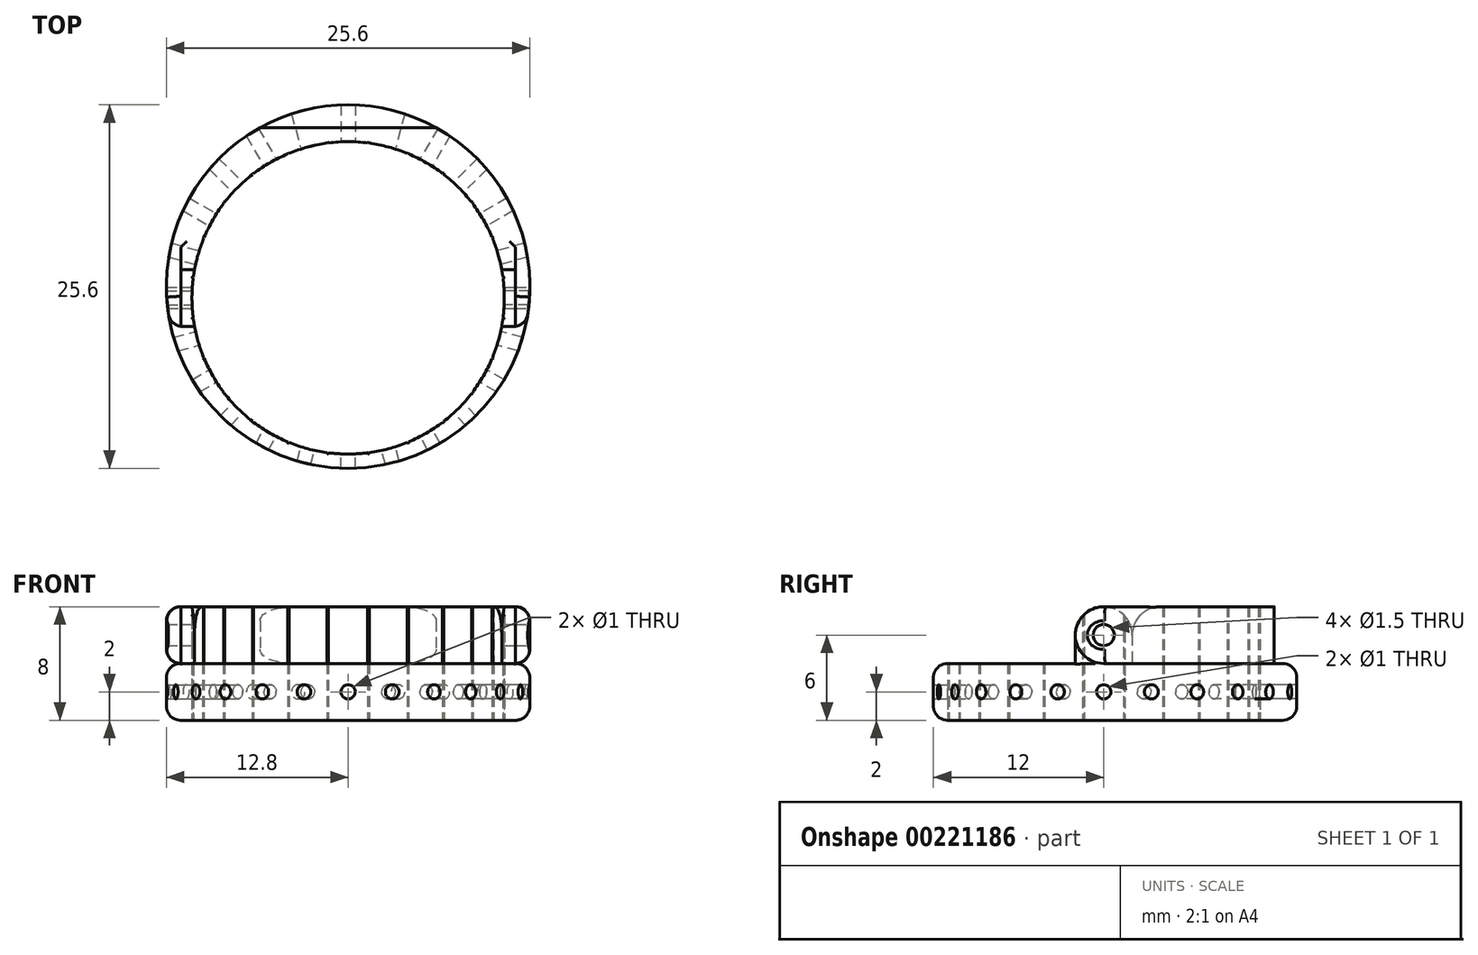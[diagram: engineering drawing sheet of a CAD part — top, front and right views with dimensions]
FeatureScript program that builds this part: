
annotation { "Feature Type Name" : "Feature", "Feature Type Description" : "" }
export const myFeature = defineFeature(function(context is Context, id is Id, definition is map)
    precondition{}
    {
        {
            var Q0;
            Q0=qCreatedBy(makeId("Top.planeOp"),FACE);
            var sketch = newSketch(context, id + "F0", { "sketchPlane" : qUnion([Q0])});
            skCircle(sketch, "E0", {"center": v(0, 0) * mm, "radius": 11 * mm});
            skCircle(sketch, "E1", {"center": v(0, 0) * mm, "radius": 12 * mm});
            skLineSegment(sketch, "E2", {"start": v(0, 0) * mm, "end": v(0, 0.8) * mm});
            skCircle(sketch, "E3", {"center": v(0, 0.8) * mm, "radius": 12.8 * mm});
            skLineSegment(sketch, "E4", {"start": v(0, 0) * mm, "end": v(-11, 0) * mm, "construction": true});
            skLineSegment(sketch, "E5", {"start": v(0, 0) * mm, "end": v(-10.9, 1.44) * mm, "construction": true});
            skLineSegment(sketch, "E6", {"start": v(-10.9, 1.44) * mm, "end": v(-11, 1.45) * mm, "construction": true});
            skLineSegment(sketch, "E7", {"start": v(-11, 1.45) * mm, "end": v(-10.9, 1.5) * mm});
            skLineSegment(sketch, "E8.MirrorCS", {"start": v(-11, 1.45) * mm, "end": v(-10.91, 1.38) * mm});
            skLineSegment(sketch, "E9.1.0", {"start": v(-11, -1.45) * mm, "end": v(-10.91, -1.38) * mm});
            skLineSegment(sketch, "E9.1.1", {"start": v(-11, -1.45) * mm, "end": v(-10.9, -1.5) * mm});
            skLineSegment(sketch, "E9.2.0", {"start": v(-10.26, -4.25) * mm, "end": v(-10.18, -4.16) * mm});
            skLineSegment(sketch, "E9.2.1", {"start": v(-10.26, -4.25) * mm, "end": v(-10.14, -4.26) * mm});
            skLineSegment(sketch, "E9.3.0", {"start": v(-8.8, -6.76) * mm, "end": v(-8.76, -6.65) * mm});
            skLineSegment(sketch, "E9.3.1", {"start": v(-8.8, -6.76) * mm, "end": v(-8.7, -6.74) * mm});
            skLineSegment(sketch, "E9.4.0", {"start": v(-6.76, -8.8) * mm, "end": v(-6.74, -8.7) * mm});
            skLineSegment(sketch, "E9.4.1", {"start": v(-6.76, -8.8) * mm, "end": v(-6.65, -8.76) * mm});
            skLineSegment(sketch, "E9.5.0", {"start": v(-4.25, -10.26) * mm, "end": v(-4.26, -10.14) * mm});
            skLineSegment(sketch, "E9.5.1", {"start": v(-4.25, -10.26) * mm, "end": v(-4.16, -10.18) * mm});
            skLineSegment(sketch, "E9.6.0", {"start": v(-1.45, -11) * mm, "end": v(-1.5, -10.9) * mm});
            skLineSegment(sketch, "E9.6.1", {"start": v(-1.45, -11) * mm, "end": v(-1.38, -10.91) * mm});
            skLineSegment(sketch, "E9.7.0", {"start": v(1.45, -11) * mm, "end": v(1.38, -10.91) * mm});
            skLineSegment(sketch, "E9.7.1", {"start": v(1.45, -11) * mm, "end": v(1.5, -10.9) * mm});
            skLineSegment(sketch, "E9.8.0", {"start": v(4.25, -10.26) * mm, "end": v(4.16, -10.18) * mm});
            skLineSegment(sketch, "E9.8.1", {"start": v(4.25, -10.26) * mm, "end": v(4.26, -10.14) * mm});
            skLineSegment(sketch, "E9.9.0", {"start": v(6.76, -8.8) * mm, "end": v(6.65, -8.76) * mm});
            skLineSegment(sketch, "E9.9.1", {"start": v(6.76, -8.8) * mm, "end": v(6.74, -8.7) * mm});
            skLineSegment(sketch, "E9.10.0", {"start": v(8.8, -6.76) * mm, "end": v(8.7, -6.74) * mm});
            skLineSegment(sketch, "E9.10.1", {"start": v(8.8, -6.76) * mm, "end": v(8.76, -6.65) * mm});
            skLineSegment(sketch, "E9.11.0", {"start": v(10.26, -4.25) * mm, "end": v(10.14, -4.26) * mm});
            skLineSegment(sketch, "E9.11.1", {"start": v(10.26, -4.25) * mm, "end": v(10.18, -4.16) * mm});
            skLineSegment(sketch, "E9.12.0", {"start": v(11, -1.45) * mm, "end": v(10.9, -1.5) * mm});
            skLineSegment(sketch, "E9.12.1", {"start": v(11, -1.45) * mm, "end": v(10.91, -1.38) * mm});
            skLineSegment(sketch, "E9.13.0", {"start": v(11, 1.45) * mm, "end": v(10.91, 1.38) * mm});
            skLineSegment(sketch, "E9.13.1", {"start": v(11, 1.45) * mm, "end": v(10.9, 1.5) * mm});
            skLineSegment(sketch, "E9.14.0", {"start": v(10.26, 4.25) * mm, "end": v(10.18, 4.16) * mm});
            skLineSegment(sketch, "E9.14.1", {"start": v(10.26, 4.25) * mm, "end": v(10.14, 4.26) * mm});
            skLineSegment(sketch, "E9.15.0", {"start": v(8.8, 6.76) * mm, "end": v(8.76, 6.65) * mm});
            skLineSegment(sketch, "E9.15.1", {"start": v(8.8, 6.76) * mm, "end": v(8.7, 6.74) * mm});
            skLineSegment(sketch, "E9.16.0", {"start": v(6.76, 8.8) * mm, "end": v(6.74, 8.7) * mm});
            skLineSegment(sketch, "E9.16.1", {"start": v(6.76, 8.8) * mm, "end": v(6.65, 8.76) * mm});
            skLineSegment(sketch, "E9.17.0", {"start": v(4.25, 10.26) * mm, "end": v(4.26, 10.14) * mm});
            skLineSegment(sketch, "E9.17.1", {"start": v(4.25, 10.26) * mm, "end": v(4.16, 10.18) * mm});
            skLineSegment(sketch, "E9.18.0", {"start": v(1.45, 11) * mm, "end": v(1.5, 10.9) * mm});
            skLineSegment(sketch, "E9.18.1", {"start": v(1.45, 11) * mm, "end": v(1.38, 10.91) * mm});
            skLineSegment(sketch, "E9.19.0", {"start": v(-1.45, 11) * mm, "end": v(-1.38, 10.91) * mm});
            skLineSegment(sketch, "E9.19.1", {"start": v(-1.45, 11) * mm, "end": v(-1.5, 10.9) * mm});
            skLineSegment(sketch, "E9.20.0", {"start": v(-4.25, 10.26) * mm, "end": v(-4.16, 10.18) * mm});
            skLineSegment(sketch, "E9.20.1", {"start": v(-4.25, 10.26) * mm, "end": v(-4.26, 10.14) * mm});
            skLineSegment(sketch, "E9.21.0", {"start": v(-6.76, 8.8) * mm, "end": v(-6.65, 8.76) * mm});
            skLineSegment(sketch, "E9.21.1", {"start": v(-6.76, 8.8) * mm, "end": v(-6.74, 8.7) * mm});
            skLineSegment(sketch, "E9.22.0", {"start": v(-8.8, 6.76) * mm, "end": v(-8.7, 6.74) * mm});
            skLineSegment(sketch, "E9.22.1", {"start": v(-8.8, 6.76) * mm, "end": v(-8.76, 6.65) * mm});
            skLineSegment(sketch, "E9.23.0", {"start": v(-10.26, 4.25) * mm, "end": v(-10.14, 4.26) * mm});
            skLineSegment(sketch, "E9.23.1", {"start": v(-10.26, 4.25) * mm, "end": v(-10.18, 4.16) * mm});
            skLineSegment(sketch, "E10.bottom", {"start": v(0, 10) * mm, "end": v(0.5, 10) * mm});
            skLineSegment(sketch, "E10.top", {"start": v(0, 14) * mm, "end": v(0.5, 14) * mm});
            skLineSegment(sketch, "E10.left", {"start": v(0, 10) * mm, "end": v(0, 14) * mm});
            skLineSegment(sketch, "E10.right", {"start": v(0.5, 10) * mm, "end": v(0.5, 14) * mm});
            skLineSegment(sketch, "E11", {"start": v(0, 0) * mm, "end": v(0, 2) * mm, "construction": true});
            skLineSegment(sketch, "E12", {"start": v(0, 2) * mm, "end": v(-10.82, 2) * mm, "construction": true});
            skLineSegment(sketch, "E13", {"start": v(-10.82, 2) * mm, "end": v(-12.74, 2) * mm});
            skLineSegment(sketch, "E14.MirrorCS", {"start": v(-10.82, -2) * mm, "end": v(-12.49, -2) * mm});
            skLineSegment(sketch, "E15.MirrorCS", {"start": v(10.82, -2) * mm, "end": v(12.49, -2) * mm});
            skLineSegment(sketch, "E16.MirrorCS", {"start": v(10.82, 2) * mm, "end": v(12.74, 2) * mm});
            skLineSegment(sketch, "E17", {"start": v(0, 12) * mm, "end": v(6.2, 12) * mm});
            skLineSegment(sketch, "E18.MirrorCS", {"start": v(0, 12) * mm, "end": v(-6.2, 12) * mm});
            skLineSegment(sketch, "E19", {"start": v(-11.78, 2) * mm, "end": v(-11.78, -2) * mm});
            skLineSegment(sketch, "E20.MirrorCS", {"start": v(11.78, 2) * mm, "end": v(11.78, -2) * mm});
            skLineSegment(sketch, "E21", {"start": v(0, 0) * mm, "end": v(0, -0.5) * mm, "construction": true});
            skLineSegment(sketch, "E22", {"start": v(0, -0.5) * mm, "end": v(-11.78, -0.5) * mm, "construction": true});
            skLineSegment(sketch, "E23", {"start": v(-11.78, -0.5) * mm, "end": v(-12.73, -0.5) * mm});
            skLineSegment(sketch, "E24", {"start": v(-11.78, 0) * mm, "end": v(-12.77, 0) * mm});
            skLineSegment(sketch, "E25.MirrorCS", {"start": v(11.78, 0) * mm, "end": v(12.77, 0) * mm});
            skLineSegment(sketch, "E26.MirrorCS", {"start": v(11.78, -0.5) * mm, "end": v(12.73, -0.5) * mm});
            skSolve(sketch);
        }
        {
            var Q0;
            {var subQ0=sQuery(id+"F0.wireOp",EDGE,"E17");var subQ1=sQuery(id+"F0.wireOp",EDGE,"E3");var subQ2=makeQuery(id+"F0.imprint","INTERSECT",VERTEX,{"derivedFrom":[subQ1,subQ0]});Q0=makeQuery(id+"F0.imprint","IMPRINT",FACE,{"disambiguationData":[TD([[makeQuery(id+"F0.imprint","IMPRINT",EDGE,{"disambiguationData":[TD([[subQ2,-1.0]])],"derivedFrom":subQ1}),1.0]])]});}
            var Q1;
            {var subQ0=sQuery(id+"F0.wireOp",EDGE,"E10.right");var subQ1=sQuery(id+"F0.wireOp",EDGE,"E3");var subQ2=makeQuery(id+"F0.imprint","INTERSECT",VERTEX,{"derivedFrom":[subQ1,subQ0]});Q1=makeQuery(id+"F0.imprint","IMPRINT",FACE,{"disambiguationData":[TD([[makeQuery(id+"F0.imprint","IMPRINT",EDGE,{"disambiguationData":[TD([[subQ2,-1.0]])],"derivedFrom":subQ1}),1.0]])]});}
            var Q2;
            {var subQ0=sQuery(id+"F0.wireOp",EDGE,"E18.MirrorCS");Q2=makeQuery(id+"F0.imprint","IMPRINT",FACE,{"disambiguationData":[TD([[makeQuery(id+"F0.imprint","IMPRINT",EDGE,{"derivedFrom":subQ0}),-1.0]])]});}
            var Q3;
            {var subQ0=sQuery(id+"F0.wireOp",EDGE,"E18.MirrorCS");Q3=makeQuery(id+"F0.imprint","IMPRINT",FACE,{"disambiguationData":[TD([[makeQuery(id+"F0.imprint","IMPRINT",EDGE,{"derivedFrom":subQ0}),1.0]])]});}
            var Q4;
            {var subQ12=sQuery(id+"F0.wireOp",EDGE,"E9.19.0");Q4=makeQuery(id+"F0.imprint","IMPRINT",FACE,{"disambiguationData":[TD([[makeQuery(id+"F0.imprint","IMPRINT",EDGE,{"derivedFrom":subQ12}),1.0]])]});}
            var Q5;
            {var subQ0=sQuery(id+"F0.wireOp",EDGE,"E16.MirrorCS");var subQ3=sQuery(id+"F0.wireOp",EDGE,"E1");var subQ4=makeQuery(id+"F0.imprint","INTERSECT",VERTEX,{"derivedFrom":[subQ3,subQ0]});Q5=makeQuery(id+"F0.imprint","IMPRINT",FACE,{"disambiguationData":[TD([[makeQuery(id+"F0.imprint","IMPRINT",EDGE,{"disambiguationData":[TD([[subQ4,-1.0]])],"derivedFrom":subQ3}),-1.0]])]});}
            var Q6;
            {var subQ1=sQuery(id+"F0.wireOp",EDGE,"E9.14.0");Q6=makeQuery(id+"F0.imprint","IMPRINT",FACE,{"disambiguationData":[TD([[makeQuery(id+"F0.imprint","IMPRINT",EDGE,{"derivedFrom":subQ1}),1.0]])]});}
            var Q7;
            {var subQ12=sQuery(id+"F0.wireOp",EDGE,"E9.12.0");Q7=makeQuery(id+"F0.imprint","IMPRINT",FACE,{"disambiguationData":[TD([[makeQuery(id+"F0.imprint","IMPRINT",EDGE,{"derivedFrom":subQ12}),1.0]])]});}
            var Q8;
            {var subQ0=sQuery(id+"F0.wireOp",EDGE,"E16.MirrorCS");var subQ1=sQuery(id+"F0.wireOp",EDGE,"E1");var subQ2=makeQuery(id+"F0.imprint","INTERSECT",VERTEX,{"derivedFrom":[subQ1,subQ0]});Q8=makeQuery(id+"F0.imprint","IMPRINT",FACE,{"disambiguationData":[TD([[makeQuery(id+"F0.imprint","IMPRINT",EDGE,{"disambiguationData":[TD([[subQ2,1.0]])],"derivedFrom":subQ1}),1.0]])]});}
            var Q9;
            {var subQ0=sQuery(id+"F0.wireOp",EDGE,"E16.MirrorCS");var subQ1=sQuery(id+"F0.wireOp",EDGE,"E1");var subQ2=makeQuery(id+"F0.imprint","INTERSECT",VERTEX,{"derivedFrom":[subQ1,subQ0]});Q9=makeQuery(id+"F0.imprint","IMPRINT",FACE,{"disambiguationData":[TD([[makeQuery(id+"F0.imprint","IMPRINT",EDGE,{"disambiguationData":[TD([[subQ2,1.0]])],"derivedFrom":subQ1}),-1.0]])]});}
            var Q10;
            {var subQ0=sQuery(id+"F0.wireOp",EDGE,"E25.MirrorCS");var subQ1=sQuery(id+"F0.wireOp",EDGE,"E1");var subQ2=makeQuery(id+"F0.imprint","INTERSECT",VERTEX,{"derivedFrom":[subQ1,subQ0]});Q10=makeQuery(id+"F0.imprint","IMPRINT",FACE,{"disambiguationData":[TD([[makeQuery(id+"F0.imprint","IMPRINT",EDGE,{"disambiguationData":[TD([[subQ2,1.0]])],"derivedFrom":subQ1}),-1.0]])]});}
            var Q11;
            {var subQ0=sQuery(id+"F0.wireOp",EDGE,"E15.MirrorCS");var subQ1=sQuery(id+"F0.wireOp",EDGE,"E1");var subQ2=makeQuery(id+"F0.imprint","INTERSECT",VERTEX,{"derivedFrom":[subQ1,subQ0]});Q11=makeQuery(id+"F0.imprint","IMPRINT",FACE,{"disambiguationData":[TD([[makeQuery(id+"F0.imprint","IMPRINT",EDGE,{"disambiguationData":[TD([[subQ2,-1.0]])],"derivedFrom":subQ1}),-1.0]])]});}
            var Q12;
            {var subQ0=sQuery(id+"F0.wireOp",EDGE,"E15.MirrorCS");var subQ1=sQuery(id+"F0.wireOp",EDGE,"E1");var subQ2=makeQuery(id+"F0.imprint","INTERSECT",VERTEX,{"derivedFrom":[subQ1,subQ0]});Q12=makeQuery(id+"F0.imprint","IMPRINT",FACE,{"disambiguationData":[TD([[makeQuery(id+"F0.imprint","IMPRINT",EDGE,{"disambiguationData":[TD([[subQ2,-1.0]])],"derivedFrom":subQ1}),1.0]])]});}
            var Q13;
            {var subQ0=sQuery(id+"F0.wireOp",EDGE,"E25.MirrorCS");var subQ1=sQuery(id+"F0.wireOp",EDGE,"E1");var subQ2=makeQuery(id+"F0.imprint","INTERSECT",VERTEX,{"derivedFrom":[subQ1,subQ0]});Q13=makeQuery(id+"F0.imprint","IMPRINT",FACE,{"disambiguationData":[TD([[makeQuery(id+"F0.imprint","IMPRINT",EDGE,{"disambiguationData":[TD([[subQ2,1.0]])],"derivedFrom":subQ1}),1.0]])]});}
            var Q14;
            {var subQ6=sQuery(id+"F0.wireOp",EDGE,"E9.2.0");Q14=makeQuery(id+"F0.imprint","IMPRINT",FACE,{"disambiguationData":[TD([[makeQuery(id+"F0.imprint","IMPRINT",EDGE,{"derivedFrom":subQ6}),1.0]])]});}
            var Q15;
            {var subQ0=sQuery(id+"F0.wireOp",EDGE,"E3");var subQ1=sQuery(id+"F0.wireOp",EDGE,"E1");var subQ2=makeQuery(id+"F0.imprint","INTERSECT",VERTEX,{"derivedFrom":[subQ1,subQ0]});Q15=makeQuery(id+"F0.imprint","IMPRINT",FACE,{"disambiguationData":[TD([[makeQuery(id+"F0.imprint","IMPRINT",EDGE,{"disambiguationData":[TD([[subQ2,-1.0]])],"derivedFrom":subQ1}),-1.0]])]});}
            var Q16;
            {var subQ0=sQuery(id+"F0.wireOp",EDGE,"E3");var subQ1=sQuery(id+"F0.wireOp",EDGE,"E1");var subQ2=makeQuery(id+"F0.imprint","INTERSECT",VERTEX,{"derivedFrom":[subQ1,subQ0]});Q16=makeQuery(id+"F0.imprint","IMPRINT",FACE,{"disambiguationData":[TD([[makeQuery(id+"F0.imprint","IMPRINT",EDGE,{"disambiguationData":[TD([[subQ2,1.0]])],"derivedFrom":subQ1}),-1.0]])]});}
            var Q17;
            {var subQ0=sQuery(id+"F0.wireOp",EDGE,"E23");var subQ1=sQuery(id+"F0.wireOp",EDGE,"E1");var subQ2=makeQuery(id+"F0.imprint","INTERSECT",VERTEX,{"derivedFrom":[subQ1,subQ0]});Q17=makeQuery(id+"F0.imprint","IMPRINT",FACE,{"disambiguationData":[TD([[makeQuery(id+"F0.imprint","IMPRINT",EDGE,{"disambiguationData":[TD([[subQ2,-1.0]])],"derivedFrom":subQ1}),-1.0]])]});}
            var Q18;
            {var subQ6=sQuery(id+"F0.wireOp",EDGE,"E7");Q18=makeQuery(id+"F0.imprint","IMPRINT",FACE,{"disambiguationData":[TD([[makeQuery(id+"F0.imprint","IMPRINT",EDGE,{"derivedFrom":subQ6}),1.0]])]});}
            var Q19;
            {var subQ0=sQuery(id+"F0.wireOp",EDGE,"E23");var subQ1=sQuery(id+"F0.wireOp",EDGE,"E1");var subQ2=makeQuery(id+"F0.imprint","INTERSECT",VERTEX,{"derivedFrom":[subQ1,subQ0]});Q19=makeQuery(id+"F0.imprint","IMPRINT",FACE,{"disambiguationData":[TD([[makeQuery(id+"F0.imprint","IMPRINT",EDGE,{"disambiguationData":[TD([[subQ2,-1.0]])],"derivedFrom":subQ1}),1.0]])]});}
            var Q20;
            {var subQ0=sQuery(id+"F0.wireOp",EDGE,"E24");var subQ1=sQuery(id+"F0.wireOp",EDGE,"E1");var subQ2=makeQuery(id+"F0.imprint","INTERSECT",VERTEX,{"derivedFrom":[subQ1,subQ0]});Q20=makeQuery(id+"F0.imprint","IMPRINT",FACE,{"disambiguationData":[TD([[makeQuery(id+"F0.imprint","IMPRINT",EDGE,{"disambiguationData":[TD([[subQ2,-1.0]])],"derivedFrom":subQ1}),1.0]])]});}
            var Q21;
            {var subQ0=sQuery(id+"F0.wireOp",EDGE,"E13");var subQ1=sQuery(id+"F0.wireOp",EDGE,"E1");var subQ2=makeQuery(id+"F0.imprint","INTERSECT",VERTEX,{"derivedFrom":[subQ1,subQ0]});Q21=makeQuery(id+"F0.imprint","IMPRINT",FACE,{"disambiguationData":[TD([[makeQuery(id+"F0.imprint","IMPRINT",EDGE,{"disambiguationData":[TD([[subQ2,-1.0]])],"derivedFrom":subQ1}),1.0]])]});}
            var Q22;
            {var subQ0=sQuery(id+"F0.wireOp",EDGE,"E13");var subQ1=sQuery(id+"F0.wireOp",EDGE,"E1");var subQ2=makeQuery(id+"F0.imprint","INTERSECT",VERTEX,{"derivedFrom":[subQ1,subQ0]});Q22=makeQuery(id+"F0.imprint","IMPRINT",FACE,{"disambiguationData":[TD([[makeQuery(id+"F0.imprint","IMPRINT",EDGE,{"disambiguationData":[TD([[subQ2,-1.0]])],"derivedFrom":subQ1}),-1.0]])]});}
            var Q23;
            {var subQ0=sQuery(id+"F0.wireOp",EDGE,"E24");var subQ1=sQuery(id+"F0.wireOp",EDGE,"E1");var subQ2=makeQuery(id+"F0.imprint","INTERSECT",VERTEX,{"derivedFrom":[subQ1,subQ0]});Q23=makeQuery(id+"F0.imprint","IMPRINT",FACE,{"disambiguationData":[TD([[makeQuery(id+"F0.imprint","IMPRINT",EDGE,{"disambiguationData":[TD([[subQ2,-1.0]])],"derivedFrom":subQ1}),-1.0]])]});}
            var Q24;
            {var subQ0=sQuery(id+"F0.wireOp",EDGE,"E10.right");var subQ1=sQuery(id+"F0.wireOp",EDGE,"E0");var subQ2=makeQuery(id+"F0.imprint","INTERSECT",VERTEX,{"derivedFrom":[subQ1,subQ0]});Q24=makeQuery(id+"F0.imprint","IMPRINT",FACE,{"disambiguationData":[TD([[makeQuery(id+"F0.imprint","IMPRINT",EDGE,{"disambiguationData":[TD([[subQ2,-1.0]])],"derivedFrom":subQ1}),-1.0]])]});}
            var Q25;
            {var subQ1=sQuery(id+"F0.wireOp",EDGE,"E1");var subQ3=sQuery(id+"F0.wireOp",EDGE,"E10.right");var subQ4=makeQuery(id+"F0.imprint","INTERSECT",VERTEX,{"derivedFrom":[subQ1,subQ3]});Q25=makeQuery(id+"F0.imprint","IMPRINT",FACE,{"disambiguationData":[TD([[makeQuery(id+"F0.imprint","IMPRINT",EDGE,{"disambiguationData":[TD([[subQ4,-1.0]])],"derivedFrom":subQ3}),1.0]])]});}
            extrude(context, id + "F1", {"entities" : qUnion([Q0, Q1, Q2, Q3, Q4, Q5, Q6, Q7, Q8, Q9, Q10, Q11, Q12, Q13, Q14, Q15, Q16, Q17, Q18, Q19, Q20, Q21, Q22, Q23, Q24, Q25]), "endBound" : BoundingType.SYMMETRIC, "depth" : 4 * mm});
        }
        {
            var Q0;
            {var subQ5=sQuery(id+"F0.wireOp",EDGE,"E10.top");Q0=makeQuery(id+"F0.imprint","IMPRINT",FACE,{"disambiguationData":[TD([[makeQuery(id+"F0.imprint","IMPRINT",EDGE,{"derivedFrom":subQ5}),-1.0]])]});}
            var Q1;
            {var subQ0=sQuery(id+"F0.wireOp",EDGE,"E10.right");var subQ1=sQuery(id+"F0.wireOp",EDGE,"E3");var subQ2=makeQuery(id+"F0.imprint","INTERSECT",VERTEX,{"derivedFrom":[subQ1,subQ0]});Q1=makeQuery(id+"F0.imprint","IMPRINT",FACE,{"disambiguationData":[TD([[makeQuery(id+"F0.imprint","IMPRINT",EDGE,{"disambiguationData":[TD([[subQ2,-1.0]])],"derivedFrom":subQ1}),1.0]])]});}
            var Q2;
            {var subQ0=sQuery(id+"F0.wireOp",EDGE,"E10.right");var subQ1=sQuery(id+"F0.wireOp",EDGE,"E0");var subQ2=makeQuery(id+"F0.imprint","INTERSECT",VERTEX,{"derivedFrom":[subQ1,subQ0]});Q2=makeQuery(id+"F0.imprint","IMPRINT",FACE,{"disambiguationData":[TD([[makeQuery(id+"F0.imprint","IMPRINT",EDGE,{"disambiguationData":[TD([[subQ2,-1.0]])],"derivedFrom":subQ1}),-1.0]])]});}
            var Q3;
            {var subQ5=sQuery(id+"F0.wireOp",EDGE,"E10.bottom");Q3=makeQuery(id+"F0.imprint","IMPRINT",FACE,{"disambiguationData":[TD([[makeQuery(id+"F0.imprint","IMPRINT",EDGE,{"derivedFrom":subQ5}),1.0]])]});}
            var Q4;
            {var subQ1=sQuery(id+"F0.wireOp",EDGE,"E1");var subQ3=sQuery(id+"F0.wireOp",EDGE,"E10.right");var subQ4=makeQuery(id+"F0.imprint","INTERSECT",VERTEX,{"derivedFrom":[subQ1,subQ3]});Q4=makeQuery(id+"F0.imprint","IMPRINT",FACE,{"disambiguationData":[TD([[makeQuery(id+"F0.imprint","IMPRINT",EDGE,{"disambiguationData":[TD([[subQ4,-1.0]])],"derivedFrom":subQ3}),1.0]])]});}
            var Q5;
            Q5=sQuery(id+"F0.wireOp",EDGE,"E10.left");
            revolve(context, id + "F2", {"entities" : qUnion([Q0, Q1, Q2, Q3, Q4]), "axis" : qUnion([Q5]), "revolveType" : RevolveType.FULL});
        }
        {
            var Q0;
            Q0=qCreatedBy(makeId("Right.planeOp"),FACE);
            var sketch = newSketch(context, id + "F3", { "sketchPlane" : qUnion([Q0])});
            skLineSegment(sketch, "E27", {"start": v(0, 0) * mm, "end": v(0, 4.13) * mm, "construction": true});
            skSolve(sketch);
        }
        {
            var Q0;
            Q0=makeQuery(id+"F2.opRevolve","SWEPT_BODY",BODY,{"disambiguationData":[OSD([sQuery(id+"F0.wireOp",EDGE,"E10.bottom"),sQuery(id+"F0.wireOp",EDGE,"E10.top"),sQuery(id+"F0.wireOp",EDGE,"E10.left"),sQuery(id+"F0.wireOp",EDGE,"E10.right")])]});
            var Q1;
            Q1=sQuery(id+"F3.wireOp",EDGE,"E27");
            circularPattern(context, id + "F4", {"operationType" : NewBodyOperationType.REMOVE, "entities" : qUnion([Q0]), "axis" : qUnion([Q1]), "angle" : 360 * degree, "instanceCount" : 24, "equalSpace" : true});
        }
        {
            var Q0;
            {var subQ6=sQuery(id+"F0.wireOp",EDGE,"E7");Q0=makeQuery(id+"F0.imprint","IMPRINT",FACE,{"disambiguationData":[TD([[makeQuery(id+"F0.imprint","IMPRINT",EDGE,{"derivedFrom":subQ6}),1.0]])]});}
            var Q1;
            {var subQ12=sQuery(id+"F0.wireOp",EDGE,"E9.12.0");Q1=makeQuery(id+"F0.imprint","IMPRINT",FACE,{"disambiguationData":[TD([[makeQuery(id+"F0.imprint","IMPRINT",EDGE,{"derivedFrom":subQ12}),1.0]])]});}
            extrude(context, id + "F5", {"entities" : qUnion([Q0, Q1]), "operationType" : NewBodyOperationType.ADD, "depth" : 6 * mm, "hasSecondDirection" : true, "secondDirectionOppositeDirection" : false, "secondDirectionDepth" : 2 * mm});
        }
        {
            var Q0;
            Q0=makeQuery(id+"F5.opExtrude","SWEPT_FACE",FACE,{"disambiguationData":[OSD([sQuery(id+"F0.wireOp",EDGE,"E20.MirrorCS")])]});
            var sketch = newSketch(context, id + "F6", { "sketchPlane" : qUnion([Q0])});
            skLineSegment(sketch, "E28", {"start": v(2, 6) * mm, "end": v(-2, 2) * mm, "construction": true});
            skLineSegment(sketch, "E29", {"start": v(2, 2) * mm, "end": v(-2, 6) * mm, "construction": true});
            skCircle(sketch, "E30", {"center": v(0, 4) * mm, "radius": 0.75 * mm});
            skSolve(sketch);
        }
        {
            var Q0;
            Q0 = qSketchRegion(id + "F6", true);
            extrude(context, id + "F7", {"entities" : qUnion([Q0]), "operationType" : NewBodyOperationType.ADD, "depth" : 1.2 * mm});
        }
        {
            var Q0;
            Q0=makeQuery(id+"F5.opExtrude","SWEPT_FACE",FACE,{"disambiguationData":[OSD([sQuery(id+"F0.wireOp",EDGE,"E19")])]});
            var sketch = newSketch(context, id + "F8", { "sketchPlane" : qUnion([Q0])});
            skLineSegment(sketch, "E31", {"start": v(2, 6) * mm, "end": v(-2, 2) * mm, "construction": true});
            skLineSegment(sketch, "E32", {"start": v(-2, 6) * mm, "end": v(2, 2) * mm, "construction": true});
            skCircle(sketch, "E33", {"center": v(0, 4) * mm, "radius": 0.75 * mm});
            skSolve(sketch);
        }
        {
            var Q0;
            Q0 = qSketchRegion(id + "F8", true);
            extrude(context, id + "F9", {"entities" : qUnion([Q0]), "operationType" : NewBodyOperationType.ADD, "depth" : 1.2 * mm});
        }
        {
            var Q0;
            {var subQ0=sQuery(id+"F0.wireOp",EDGE,"E15.MirrorCS");var subQ1=sQuery(id+"F0.wireOp",EDGE,"E1");var subQ2=makeQuery(id+"F0.imprint","INTERSECT",VERTEX,{"derivedFrom":[subQ1,subQ0]});Q0=makeQuery(id+"F0.imprint","IMPRINT",FACE,{"disambiguationData":[TD([[makeQuery(id+"F0.imprint","IMPRINT",EDGE,{"disambiguationData":[TD([[subQ2,-1.0]])],"derivedFrom":subQ1}),-1.0]])]});}
            var Q1;
            {var subQ0=sQuery(id+"F0.wireOp",EDGE,"E25.MirrorCS");var subQ1=sQuery(id+"F0.wireOp",EDGE,"E1");var subQ2=makeQuery(id+"F0.imprint","INTERSECT",VERTEX,{"derivedFrom":[subQ1,subQ0]});Q1=makeQuery(id+"F0.imprint","IMPRINT",FACE,{"disambiguationData":[TD([[makeQuery(id+"F0.imprint","IMPRINT",EDGE,{"disambiguationData":[TD([[subQ2,1.0]])],"derivedFrom":subQ1}),-1.0]])]});}
            var Q2;
            {var subQ0=sQuery(id+"F0.wireOp",EDGE,"E16.MirrorCS");var subQ1=sQuery(id+"F0.wireOp",EDGE,"E1");var subQ2=makeQuery(id+"F0.imprint","INTERSECT",VERTEX,{"derivedFrom":[subQ1,subQ0]});Q2=makeQuery(id+"F0.imprint","IMPRINT",FACE,{"disambiguationData":[TD([[makeQuery(id+"F0.imprint","IMPRINT",EDGE,{"disambiguationData":[TD([[subQ2,1.0]])],"derivedFrom":subQ1}),-1.0]])]});}
            var Q3;
            {var subQ0=sQuery(id+"F0.wireOp",EDGE,"E16.MirrorCS");var subQ3=sQuery(id+"F0.wireOp",EDGE,"E1");var subQ4=makeQuery(id+"F0.imprint","INTERSECT",VERTEX,{"derivedFrom":[subQ3,subQ0]});Q3=makeQuery(id+"F0.imprint","IMPRINT",FACE,{"disambiguationData":[TD([[makeQuery(id+"F0.imprint","IMPRINT",EDGE,{"disambiguationData":[TD([[subQ4,-1.0]])],"derivedFrom":subQ3}),-1.0]])]});}
            var Q4;
            {var subQ1=sQuery(id+"F0.wireOp",EDGE,"E9.14.0");Q4=makeQuery(id+"F0.imprint","IMPRINT",FACE,{"disambiguationData":[TD([[makeQuery(id+"F0.imprint","IMPRINT",EDGE,{"derivedFrom":subQ1}),1.0]])]});}
            var Q5;
            {var subQ0=sQuery(id+"F0.wireOp",EDGE,"E15.MirrorCS");var subQ1=sQuery(id+"F0.wireOp",EDGE,"E1");var subQ2=makeQuery(id+"F0.imprint","INTERSECT",VERTEX,{"derivedFrom":[subQ1,subQ0]});Q5=makeQuery(id+"F0.imprint","IMPRINT",FACE,{"disambiguationData":[TD([[makeQuery(id+"F0.imprint","IMPRINT",EDGE,{"disambiguationData":[TD([[subQ2,-1.0]])],"derivedFrom":subQ1}),1.0]])]});}
            var Q6;
            {var subQ0=sQuery(id+"F0.wireOp",EDGE,"E16.MirrorCS");var subQ1=sQuery(id+"F0.wireOp",EDGE,"E1");var subQ2=makeQuery(id+"F0.imprint","INTERSECT",VERTEX,{"derivedFrom":[subQ1,subQ0]});Q6=makeQuery(id+"F0.imprint","IMPRINT",FACE,{"disambiguationData":[TD([[makeQuery(id+"F0.imprint","IMPRINT",EDGE,{"disambiguationData":[TD([[subQ2,1.0]])],"derivedFrom":subQ1}),1.0]])]});}
            var Q7;
            {var subQ0=sQuery(id+"F0.wireOp",EDGE,"E10.right");var subQ1=sQuery(id+"F0.wireOp",EDGE,"E0");var subQ2=makeQuery(id+"F0.imprint","INTERSECT",VERTEX,{"derivedFrom":[subQ1,subQ0]});Q7=makeQuery(id+"F0.imprint","IMPRINT",FACE,{"disambiguationData":[TD([[makeQuery(id+"F0.imprint","IMPRINT",EDGE,{"disambiguationData":[TD([[subQ2,-1.0]])],"derivedFrom":subQ1}),-1.0]])]});}
            var Q8;
            {var subQ12=sQuery(id+"F0.wireOp",EDGE,"E9.19.0");Q8=makeQuery(id+"F0.imprint","IMPRINT",FACE,{"disambiguationData":[TD([[makeQuery(id+"F0.imprint","IMPRINT",EDGE,{"derivedFrom":subQ12}),1.0]])]});}
            var Q9;
            {var subQ0=sQuery(id+"F0.wireOp",EDGE,"E18.MirrorCS");Q9=makeQuery(id+"F0.imprint","IMPRINT",FACE,{"disambiguationData":[TD([[makeQuery(id+"F0.imprint","IMPRINT",EDGE,{"derivedFrom":subQ0}),1.0]])]});}
            var Q10;
            {var subQ0=sQuery(id+"F0.wireOp",EDGE,"E23");var subQ1=sQuery(id+"F0.wireOp",EDGE,"E1");var subQ2=makeQuery(id+"F0.imprint","INTERSECT",VERTEX,{"derivedFrom":[subQ1,subQ0]});Q10=makeQuery(id+"F0.imprint","IMPRINT",FACE,{"disambiguationData":[TD([[makeQuery(id+"F0.imprint","IMPRINT",EDGE,{"disambiguationData":[TD([[subQ2,-1.0]])],"derivedFrom":subQ1}),-1.0]])]});}
            var Q11;
            {var subQ0=sQuery(id+"F0.wireOp",EDGE,"E23");var subQ1=sQuery(id+"F0.wireOp",EDGE,"E1");var subQ2=makeQuery(id+"F0.imprint","INTERSECT",VERTEX,{"derivedFrom":[subQ1,subQ0]});Q11=makeQuery(id+"F0.imprint","IMPRINT",FACE,{"disambiguationData":[TD([[makeQuery(id+"F0.imprint","IMPRINT",EDGE,{"disambiguationData":[TD([[subQ2,-1.0]])],"derivedFrom":subQ1}),1.0]])]});}
            var Q12;
            {var subQ0=sQuery(id+"F0.wireOp",EDGE,"E24");var subQ1=sQuery(id+"F0.wireOp",EDGE,"E1");var subQ2=makeQuery(id+"F0.imprint","INTERSECT",VERTEX,{"derivedFrom":[subQ1,subQ0]});Q12=makeQuery(id+"F0.imprint","IMPRINT",FACE,{"disambiguationData":[TD([[makeQuery(id+"F0.imprint","IMPRINT",EDGE,{"disambiguationData":[TD([[subQ2,-1.0]])],"derivedFrom":subQ1}),-1.0]])]});}
            var Q13;
            {var subQ0=sQuery(id+"F0.wireOp",EDGE,"E24");var subQ1=sQuery(id+"F0.wireOp",EDGE,"E1");var subQ2=makeQuery(id+"F0.imprint","INTERSECT",VERTEX,{"derivedFrom":[subQ1,subQ0]});Q13=makeQuery(id+"F0.imprint","IMPRINT",FACE,{"disambiguationData":[TD([[makeQuery(id+"F0.imprint","IMPRINT",EDGE,{"disambiguationData":[TD([[subQ2,-1.0]])],"derivedFrom":subQ1}),1.0]])]});}
            var Q14;
            {var subQ0=sQuery(id+"F0.wireOp",EDGE,"E13");var subQ1=sQuery(id+"F0.wireOp",EDGE,"E1");var subQ2=makeQuery(id+"F0.imprint","INTERSECT",VERTEX,{"derivedFrom":[subQ1,subQ0]});Q14=makeQuery(id+"F0.imprint","IMPRINT",FACE,{"disambiguationData":[TD([[makeQuery(id+"F0.imprint","IMPRINT",EDGE,{"disambiguationData":[TD([[subQ2,-1.0]])],"derivedFrom":subQ1}),-1.0]])]});}
            var Q15;
            {var subQ0=sQuery(id+"F0.wireOp",EDGE,"E13");var subQ1=sQuery(id+"F0.wireOp",EDGE,"E1");var subQ2=makeQuery(id+"F0.imprint","INTERSECT",VERTEX,{"derivedFrom":[subQ1,subQ0]});Q15=makeQuery(id+"F0.imprint","IMPRINT",FACE,{"disambiguationData":[TD([[makeQuery(id+"F0.imprint","IMPRINT",EDGE,{"disambiguationData":[TD([[subQ2,-1.0]])],"derivedFrom":subQ1}),1.0]])]});}
            var Q16;
            {var subQ0=sQuery(id+"F0.wireOp",EDGE,"E25.MirrorCS");var subQ1=sQuery(id+"F0.wireOp",EDGE,"E1");var subQ2=makeQuery(id+"F0.imprint","INTERSECT",VERTEX,{"derivedFrom":[subQ1,subQ0]});Q16=makeQuery(id+"F0.imprint","IMPRINT",FACE,{"disambiguationData":[TD([[makeQuery(id+"F0.imprint","IMPRINT",EDGE,{"disambiguationData":[TD([[subQ2,1.0]])],"derivedFrom":subQ1}),1.0]])]});}
            var Q17;
            {var subQ1=sQuery(id+"F0.wireOp",EDGE,"E1");var subQ3=sQuery(id+"F0.wireOp",EDGE,"E10.right");var subQ4=makeQuery(id+"F0.imprint","INTERSECT",VERTEX,{"derivedFrom":[subQ1,subQ3]});Q17=makeQuery(id+"F0.imprint","IMPRINT",FACE,{"disambiguationData":[TD([[makeQuery(id+"F0.imprint","IMPRINT",EDGE,{"disambiguationData":[TD([[subQ4,-1.0]])],"derivedFrom":subQ3}),1.0]])]});}
            extrude(context, id + "F10", {"entities" : qUnion([Q0, Q1, Q2, Q3, Q4, Q5, Q6, Q7, Q8, Q9, Q10, Q11, Q12, Q13, Q14, Q15, Q16, Q17]), "depth" : 6 * mm, "hasSecondDirection" : true, "secondDirectionOppositeDirection" : false, "secondDirectionDepth" : 2 * mm});
        }
        {
            var Q0;
            Q0=makeQuery(id+"F5.opExtrude","CAP_EDGE",EDGE,{"disambiguationData":[OSD([sQuery(id+"F0.wireOp",EDGE,"E14.MirrorCS")])],"isStart":false});
            var Q1;
            Q1=makeQuery(id+"F5.opExtrude","CAP_EDGE",EDGE,{"disambiguationData":[OSD([sQuery(id+"F0.wireOp",EDGE,"E13")])],"isStart":false});
            var Q2;
            Q2=makeQuery(id+"F5.opExtrude","CAP_EDGE",EDGE,{"disambiguationData":[OSD([sQuery(id+"F0.wireOp",EDGE,"E16.MirrorCS")])],"isStart":false});
            var Q3;
            Q3=makeQuery(id+"F5.opExtrude","CAP_EDGE",EDGE,{"disambiguationData":[OSD([sQuery(id+"F0.wireOp",EDGE,"E15.MirrorCS")])],"isStart":false});
            var Q4;
            Q4=makeQuery(id+"F10.opExtrude","CAP_EDGE",EDGE,{"disambiguationData":[OSD([sQuery(id+"F0.wireOp",EDGE,"E15.MirrorCS")])],"isStart":true});
            var Q5;
            Q5=makeQuery(id+"F10.opExtrude","CAP_EDGE",EDGE,{"disambiguationData":[OSD([sQuery(id+"F0.wireOp",EDGE,"E15.MirrorCS")])],"isStart":false});
            var Q6;
            Q6=makeQuery(id+"F10.opExtrude","CAP_EDGE",EDGE,{"disambiguationData":[OSD([sQuery(id+"F0.wireOp",EDGE,"E14.MirrorCS")])],"isStart":true});
            var Q7;
            Q7=makeQuery(id+"F10.opExtrude","CAP_EDGE",EDGE,{"disambiguationData":[OSD([sQuery(id+"F0.wireOp",EDGE,"E14.MirrorCS")])],"isStart":false});
            var Q8;
            Q8=makeQuery(id+"F10.opExtrude","CAP_EDGE",EDGE,{"disambiguationData":[OSD([sQuery(id+"F0.wireOp",EDGE,"E16.MirrorCS")])],"isStart":false});
            var Q9;
            Q9=makeQuery(id+"F10.opExtrude","CAP_EDGE",EDGE,{"disambiguationData":[OSD([sQuery(id+"F0.wireOp",EDGE,"E13")])],"isStart":false});
            fillet(context, id + "F11", {"entities" : qUnion([Q0, Q1, Q2, Q3, Q4, Q5, Q6, Q7, Q8, Q9]), "radius" : 2 * mm, "tangentPropagation" : true, "allowEdgeOverflow" : false});
        }
        {
            var Q0;
            {var subQ0=sQuery(id+"F0.wireOp",EDGE,"E3");var subQ1=makeQuery(id+"F0.imprint","INTERSECT",VERTEX,{"derivedFrom":[subQ0,sQuery(id+"F0.wireOp",EDGE,"E16.MirrorCS")]});var subQ2=makeQuery(id+"F0.imprint","INTERSECT",VERTEX,{"derivedFrom":[subQ0,sQuery(id+"F0.wireOp",EDGE,"E25.MirrorCS")]});var subQ4=sQuery(id+"F0.wireOp",EDGE,"E15.MirrorCS");Q0=makeQuery(id+"F11.opFillet","BLEND_EDGE",EDGE,{"blendedFrom":[makeQuery(id+"F10.opExtrude","CAP_EDGE",EDGE,{"disambiguationData":[OSD([subQ4])],"isStart":false}),makeQuery(id+"F10.opExtrude","SWEPT_FACE",FACE,{"disambiguationData":[OSD([subQ0]),TDD([makeQuery(id+"F0.imprint","IMPRINT",EDGE,{"disambiguationData":[TD([[subQ1,-1.0]])],"derivedFrom":subQ0}),makeQuery(id+"F0.imprint","IMPRINT",EDGE,{"disambiguationData":[TD([[makeQuery(id+"F0.imprint","INTERSECT",VERTEX,{"derivedFrom":[subQ0,subQ4]}),-1.0]])],"derivedFrom":subQ0}),makeQuery(id+"F0.imprint","IMPRINT",EDGE,{"disambiguationData":[TD([[subQ2,1.0]])],"derivedFrom":subQ0}),makeQuery(id+"F0.imprint","IMPRINT",EDGE,{"disambiguationData":[TD([[subQ1,1.0]])],"derivedFrom":subQ0})])]})],"blendedInto":[makeQuery(id+"F10.opExtrude","SWEPT_FACE",FACE,{"disambiguationData":[OSD([subQ0]),TDD([makeQuery(id+"F0.imprint","IMPRINT",EDGE,{"disambiguationData":[TD([[subQ1,-1.0]])],"derivedFrom":subQ0}),makeQuery(id+"F0.imprint","IMPRINT",EDGE,{"disambiguationData":[TD([[makeQuery(id+"F0.imprint","INTERSECT",VERTEX,{"derivedFrom":[subQ0,subQ4]}),-1.0]])],"derivedFrom":subQ0}),makeQuery(id+"F0.imprint","IMPRINT",EDGE,{"disambiguationData":[TD([[subQ2,1.0]])],"derivedFrom":subQ0}),makeQuery(id+"F0.imprint","IMPRINT",EDGE,{"disambiguationData":[TD([[subQ1,1.0]])],"derivedFrom":subQ0})])]})]});}
            var Q1;
            {var subQ0=sQuery(id+"F0.wireOp",EDGE,"E3");var subQ1=makeQuery(id+"F0.imprint","INTERSECT",VERTEX,{"derivedFrom":[subQ0,sQuery(id+"F0.wireOp",EDGE,"E16.MirrorCS")]});var subQ2=makeQuery(id+"F0.imprint","INTERSECT",VERTEX,{"derivedFrom":[subQ0,sQuery(id+"F0.wireOp",EDGE,"E25.MirrorCS")]});var subQ4=sQuery(id+"F0.wireOp",EDGE,"E15.MirrorCS");Q1=makeQuery(id+"F11.opFillet","BLEND_EDGE",EDGE,{"blendedFrom":[makeQuery(id+"F10.opExtrude","CAP_EDGE",EDGE,{"disambiguationData":[OSD([subQ4])],"isStart":true}),makeQuery(id+"F10.opExtrude","SWEPT_FACE",FACE,{"disambiguationData":[OSD([subQ0]),TDD([makeQuery(id+"F0.imprint","IMPRINT",EDGE,{"disambiguationData":[TD([[subQ1,-1.0]])],"derivedFrom":subQ0}),makeQuery(id+"F0.imprint","IMPRINT",EDGE,{"disambiguationData":[TD([[makeQuery(id+"F0.imprint","INTERSECT",VERTEX,{"derivedFrom":[subQ0,subQ4]}),-1.0]])],"derivedFrom":subQ0}),makeQuery(id+"F0.imprint","IMPRINT",EDGE,{"disambiguationData":[TD([[subQ2,1.0]])],"derivedFrom":subQ0}),makeQuery(id+"F0.imprint","IMPRINT",EDGE,{"disambiguationData":[TD([[subQ1,1.0]])],"derivedFrom":subQ0})])]})],"blendedInto":[makeQuery(id+"F10.opExtrude","SWEPT_FACE",FACE,{"disambiguationData":[OSD([subQ0]),TDD([makeQuery(id+"F0.imprint","IMPRINT",EDGE,{"disambiguationData":[TD([[subQ1,-1.0]])],"derivedFrom":subQ0}),makeQuery(id+"F0.imprint","IMPRINT",EDGE,{"disambiguationData":[TD([[makeQuery(id+"F0.imprint","INTERSECT",VERTEX,{"derivedFrom":[subQ0,subQ4]}),-1.0]])],"derivedFrom":subQ0}),makeQuery(id+"F0.imprint","IMPRINT",EDGE,{"disambiguationData":[TD([[subQ2,1.0]])],"derivedFrom":subQ0}),makeQuery(id+"F0.imprint","IMPRINT",EDGE,{"disambiguationData":[TD([[subQ1,1.0]])],"derivedFrom":subQ0})])]})]});}
            var Q2;
            {var subQ0=sQuery(id+"F0.wireOp",EDGE,"E14.MirrorCS");var subQ1=sQuery(id+"F0.wireOp",EDGE,"E3");var subQ2=makeQuery(id+"F0.imprint","INTERSECT",VERTEX,{"derivedFrom":[subQ1,sQuery(id+"F0.wireOp",EDGE,"E23")]});var subQ4=makeQuery(id+"F0.imprint","INTERSECT",VERTEX,{"derivedFrom":[subQ1,sQuery(id+"F0.wireOp",EDGE,"E13")]});Q2=makeQuery(id+"F11.opFillet","BLEND_EDGE",EDGE,{"blendedFrom":[makeQuery(id+"F10.opExtrude","CAP_EDGE",EDGE,{"disambiguationData":[OSD([subQ0])],"isStart":false}),makeQuery(id+"F10.opExtrude","SWEPT_FACE",FACE,{"disambiguationData":[OSD([subQ1]),TDD([makeQuery(id+"F0.imprint","IMPRINT",EDGE,{"disambiguationData":[TD([[subQ4,1.0]])],"derivedFrom":subQ1}),makeQuery(id+"F0.imprint","IMPRINT",EDGE,{"disambiguationData":[TD([[subQ4,-1.0]])],"derivedFrom":subQ1}),makeQuery(id+"F0.imprint","IMPRINT",EDGE,{"disambiguationData":[TD([[subQ2,1.0]])],"derivedFrom":subQ1}),makeQuery(id+"F0.imprint","IMPRINT",EDGE,{"disambiguationData":[TD([[makeQuery(id+"F0.imprint","INTERSECT",VERTEX,{"derivedFrom":[subQ1,subQ0]}),1.0]])],"derivedFrom":subQ1})])]})],"blendedInto":[makeQuery(id+"F10.opExtrude","SWEPT_FACE",FACE,{"disambiguationData":[OSD([subQ1]),TDD([makeQuery(id+"F0.imprint","IMPRINT",EDGE,{"disambiguationData":[TD([[subQ4,1.0]])],"derivedFrom":subQ1}),makeQuery(id+"F0.imprint","IMPRINT",EDGE,{"disambiguationData":[TD([[subQ4,-1.0]])],"derivedFrom":subQ1}),makeQuery(id+"F0.imprint","IMPRINT",EDGE,{"disambiguationData":[TD([[subQ2,1.0]])],"derivedFrom":subQ1}),makeQuery(id+"F0.imprint","IMPRINT",EDGE,{"disambiguationData":[TD([[makeQuery(id+"F0.imprint","INTERSECT",VERTEX,{"derivedFrom":[subQ1,subQ0]}),1.0]])],"derivedFrom":subQ1})])]})]});}
            var Q3;
            Q3=makeQuery(id+"F1.opExtrude","CAP_EDGE",EDGE,{"disambiguationData":[OSD([sQuery(id+"F0.wireOp",EDGE,"E3")])],"isStart":true});
            var Q4;
            Q4=makeQuery(id+"F1.opExtrude","CAP_EDGE",EDGE,{"disambiguationData":[OSD([sQuery(id+"F0.wireOp",EDGE,"E3")])],"isStart":false});
            fillet(context, id + "F12", {"entities" : qUnion([Q0, Q1, Q2, Q3, Q4]), "radius" : 1 * mm, "tangentPropagation" : true, "allowEdgeOverflow" : false});
        }
        {
            var Q0;
            Q0 = qSketchRegion(id + "F8", true);
            extrude(context, id + "F13", {"entities" : qUnion([Q0]), "operationType" : NewBodyOperationType.REMOVE, "endBound" : BoundingType.SYMMETRIC, "depth" : 66 * mm});
        }
    });
